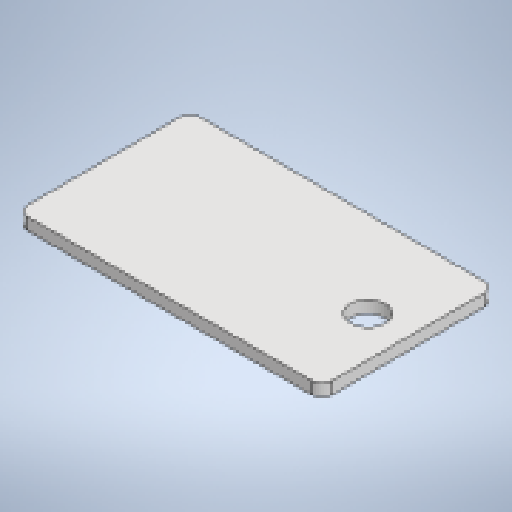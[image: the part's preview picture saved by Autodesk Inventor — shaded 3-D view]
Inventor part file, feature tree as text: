
AUTODESK INVENTOR PART (.ipt)
format: ipt  version: 2025.3 (Build 293356030, 356C)  size: 161,792 bytes
history: native  units: mm
features: other x2, sheet_metal_op x1, chamfer x1, sketch x1
ambient origin geometry x8: Origin, YZ Plane, XZ Plane, XY Plane, X Axis, Y Axis, Z Axis, Center Point
bodies: Solid1 (feature_tree)
feature tree (5):
  sheet_metal_op  "Face1"
  chamfer  "Corner Round2"
  sketch  "Sketch1"  dims[d0=150.0mm d1=90.0mm d2=6.0mm d23=17.0mm d25=20.0mm d26=20.0mm d33=5.0mm]
  other  "Plate1"
  other  "Definition1"
